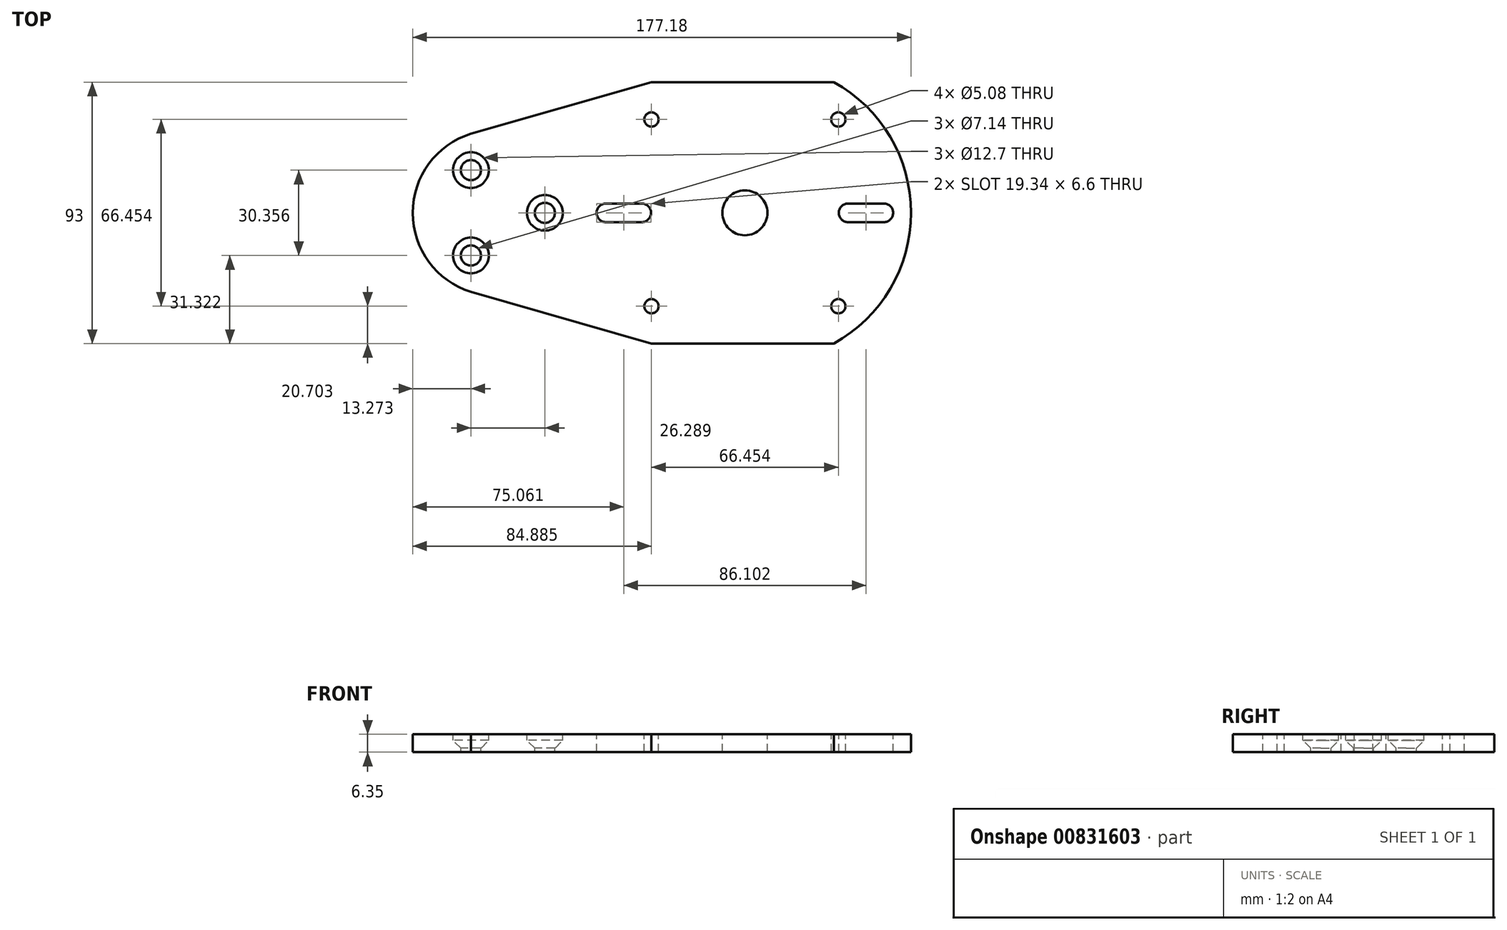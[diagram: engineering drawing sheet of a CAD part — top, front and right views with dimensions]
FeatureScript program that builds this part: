
annotation { "Feature Type Name" : "Feature", "Feature Type Description" : "" }
export const myFeature = defineFeature(function(context is Context, id is Id, definition is map)
    precondition{}
    {
        {
            var Q0;
            Q0=qCreatedBy(makeId("Top.planeOp"),FACE);
            var sketch = newSketch(context, id + "F0", { "sketchPlane" : qUnion([Q0])});
            skLineSegment(sketch, "E0", {"start": v(0, 0) * mm, "end": v(-58.93, 0) * mm, "construction": true});
            skPoint(sketch, "E1", {"position": v(-29.46, 0) * mm});
            skCircle(sketch, "E2", {"center": v(-29.46, 0) * mm, "radius": 29.46 * mm, "construction": true});
            skCircle(sketch, "E3", {"center": v(-29.46, 0) * mm, "radius": 17.53 * mm, "construction": true});
            skPoint(sketch, "E4", {"position": v(59.18, 0) * mm});
            skPoint(sketch, "E5", {"position": v(-11.94, 0) * mm});
            skCircle(sketch, "E6", {"center": v(59.18, 0) * mm, "radius": 19.05 * mm, "construction": true});
            skCircle(sketch, "E7", {"center": v(59.18, 0) * mm, "radius": 31.75 * mm, "construction": true});
            skCircle(sketch, "E8", {"center": v(-11.94, 0) * mm, "radius": 3.57 * mm});
            skCircle(sketch, "E9", {"center": v(-29.46, 0) * mm, "radius": 10.16 * mm, "construction": true});
            skArc(sketch, "E10", {"start": v(92.4, -46.5) * mm, "mid": v(116.33, 0) * mm, "end": v(92.4, 46.5) * mm, "construction": true});
            skPoint(sketch, "E11", {"position": v(59.18, 57.15) * mm});
            skPoint(sketch, "E12", {"position": v(59.18, -57.15) * mm});
            skLineSegment(sketch, "E13", {"start": v(90.93, 0) * mm, "end": v(118.25, 0) * mm, "construction": true});
            skCircle(sketch, "E14", {"center": v(59.18, 0) * mm, "radius": 47 * mm, "construction": true});
            skLineSegment(sketch, "E15", {"start": v(59.18, 0) * mm, "end": v(90.93, 0) * mm, "construction": true});
            skLineSegment(sketch, "E16", {"start": v(59.18, 0) * mm, "end": v(99.6, 40.41) * mm, "construction": true});
            skCircle(sketch, "E17", {"center": v(92.4, 33.23) * mm, "radius": 2.54 * mm});
            skCircle(sketch, "E18.2.0", {"center": v(25.96, 33.23) * mm, "radius": 2.54 * mm});
            skCircle(sketch, "E19", {"center": v(59.18, 0) * mm, "radius": 8 * mm});
            skCircle(sketch, "E20.1.4.0", {"center": v(25.96, -33.23) * mm, "radius": 2.54 * mm});
            skCircle(sketch, "E20.1.6.0", {"center": v(92.4, -33.23) * mm, "radius": 2.54 * mm});
            skPoint(sketch, "E21", {"position": v(25.96, 46.5) * mm});
            skPoint(sketch, "E22", {"position": v(25.96, -46.5) * mm});
            skLineSegment(sketch, "E23", {"start": v(25.96, 46.5) * mm, "end": v(90.78, 46.5) * mm});
            skLineSegment(sketch, "E24", {"start": v(25.96, -46.5) * mm, "end": v(90.78, -46.5) * mm});
            skArc(sketch, "E25.converted", {"start": v(92.4, 46.5) * mm, "mid": v(2.03, 0) * mm, "end": v(92.4, -46.5) * mm, "construction": true});
            skLineSegment(sketch, "E26", {"start": v(59.18, 0) * mm, "end": v(99.6, -40.41) * mm, "construction": true});
            skArc(sketch, "E27", {"start": v(90.78, -46.5) * mm, "mid": v(118.25, 0) * mm, "end": v(90.78, 46.5) * mm});
            skCircle(sketch, "E28", {"center": v(59.18, 0) * mm, "radius": 36.83 * mm, "construction": true});
            skCircle(sketch, "E29", {"center": v(59.18, 0) * mm, "radius": 49.53 * mm, "construction": true});
            skLineSegment(sketch, "E30", {"start": v(95.86, 3.3) * mm, "end": v(108.6, 3.3) * mm});
            skLineSegment(sketch, "E31", {"start": v(95.86, -3.3) * mm, "end": v(108.6, -3.3) * mm});
            skArc(sketch, "E32", {"start": v(108.6, 3.3) * mm, "mid": v(111.9, 0) * mm, "end": v(108.6, -3.3) * mm});
            skArc(sketch, "E33", {"start": v(95.86, 3.3) * mm, "mid": v(92.56, 0) * mm, "end": v(95.86, -3.3) * mm});
            skLineSegment(sketch, "E34.1.0", {"start": v(22.5, -3.3) * mm, "end": v(9.76, -3.3) * mm});
            skArc(sketch, "E34.1.1", {"start": v(22.5, -3.3) * mm, "mid": v(25.8, 0) * mm, "end": v(22.5, 3.3) * mm});
            skLineSegment(sketch, "E34.1.2", {"start": v(22.5, 3.3) * mm, "end": v(9.76, 3.3) * mm});
            skArc(sketch, "E34.1.3", {"start": v(9.76, -3.3) * mm, "mid": v(6.46, 0) * mm, "end": v(9.76, 3.3) * mm});
            skPoint(sketch, "E35", {"position": v(-38.23, 28.13) * mm});
            skLineSegment(sketch, "E36", {"start": v(25.96, 46.5) * mm, "end": v(-38.23, 28.13) * mm});
            skPoint(sketch, "E37", {"position": v(-38.23, -28.13) * mm});
            skLineSegment(sketch, "E38", {"start": v(25.96, -46.5) * mm, "end": v(-38.23, -28.13) * mm});
            skArc(sketch, "E39", {"start": v(-38.23, 28.13) * mm, "mid": v(-58.93, 0) * mm, "end": v(-38.23, -28.13) * mm});
            skCircle(sketch, "E40.1.0", {"center": v(-38.23, 15.18) * mm, "radius": 3.57 * mm});
            skCircle(sketch, "E40.2.0", {"center": v(-38.23, -15.18) * mm, "radius": 3.57 * mm});
            skSolve(sketch);
        }
        {
            var Q0;
            Q0=makeQuery(id+"F0.imprint","IMPRINT",FACE,{"disambiguationData":[TD([[makeQuery(id+"F0.imprint","IMPRINT",EDGE,{"derivedFrom":sQuery(id+"F0.wireOp",EDGE,"E8")}),-1.0]])]});
            extrude(context, id + "F1", {"entities" : qUnion([Q0]), "oppositeDirection" : true, "depth" : 6.35 * mm, "offsetDistance" : 25.4 * mm});
        }
        {
            var Q0;
            Q0=makeQuery(id+"F1.opExtrude","CAP_FACE",FACE,{"disambiguationData":[OSD([sQuery(id+"F0.wireOp",EDGE,"E8"),sQuery(id+"F0.wireOp",EDGE,"E17"),sQuery(id+"F0.wireOp",EDGE,"E18.2.0"),sQuery(id+"F0.wireOp",EDGE,"E19"),sQuery(id+"F0.wireOp",EDGE,"E20.1.4.0"),sQuery(id+"F0.wireOp",EDGE,"E20.1.6.0"),sQuery(id+"F0.wireOp",EDGE,"E23"),sQuery(id+"F0.wireOp",EDGE,"E24"),sQuery(id+"F0.wireOp",EDGE,"E27"),sQuery(id+"F0.wireOp",EDGE,"E30"),sQuery(id+"F0.wireOp",EDGE,"E31"),sQuery(id+"F0.wireOp",EDGE,"E32"),sQuery(id+"F0.wireOp",EDGE,"E33"),sQuery(id+"F0.wireOp",EDGE,"E34.1.0"),sQuery(id+"F0.wireOp",EDGE,"E34.1.1"),sQuery(id+"F0.wireOp",EDGE,"E34.1.2"),sQuery(id+"F0.wireOp",EDGE,"E34.1.3"),sQuery(id+"F0.wireOp",EDGE,"E36"),sQuery(id+"F0.wireOp",EDGE,"E38"),sQuery(id+"F0.wireOp",EDGE,"E39"),sQuery(id+"F0.wireOp",EDGE,"E40.1.0"),sQuery(id+"F0.wireOp",EDGE,"E40.2.0")])],"isStart":false});
            cPlane(context, id + "F2", {"entities" : qUnion([Q0]), "cplaneType" : CPlaneType.OFFSET, "offset" : 1.4 * mm, "oppositeDirection" : true, "width" : 152.4 * mm, "height" : 152.4 * mm});
        }
        {
            var Q0;
            Q0=qCreatedBy(id+"F2.planeOp",FACE);
            var sketch = newSketch(context, id + "F3", { "sketchPlane" : qUnion([Q0])});
            skCircle(sketch, "E41", {"center": v(-29.46, 0) * mm, "radius": 17.53 * mm, "construction": true});
            skCircle(sketch, "E42", {"center": v(-11.94, 0) * mm, "radius": 3.57 * mm});
            skCircle(sketch, "E43.1.0", {"center": v(-38.23, 15.18) * mm, "radius": 3.57 * mm});
            skCircle(sketch, "E43.2.0", {"center": v(-38.23, -15.18) * mm, "radius": 3.57 * mm});
            skSolve(sketch);
        }
        {
            var Q0;
            Q0=makeQuery(id+"F3.imprint","IMPRINT",FACE,{"disambiguationData":[TD([[makeQuery(id+"F3.imprint","IMPRINT",EDGE,{"derivedFrom":sQuery(id+"F3.wireOp",EDGE,"E43.1.0")}),1.0]])]});
            var Q1;
            Q1=makeQuery(id+"F3.imprint","IMPRINT",FACE,{"disambiguationData":[TD([[makeQuery(id+"F3.imprint","IMPRINT",EDGE,{"derivedFrom":sQuery(id+"F3.wireOp",EDGE,"E43.2.0")}),1.0]])]});
            var Q2;
            Q2=makeQuery(id+"F3.imprint","IMPRINT",FACE,{"disambiguationData":[TD([[makeQuery(id+"F3.imprint","IMPRINT",EDGE,{"derivedFrom":sQuery(id+"F3.wireOp",EDGE,"E42")}),1.0]])]});
            var Q3;
            Q3=makeQuery(id+"F1.opExtrude","CAP_FACE",FACE,{"disambiguationData":[OSD([sQuery(id+"F0.wireOp",EDGE,"E8"),sQuery(id+"F0.wireOp",EDGE,"E17"),sQuery(id+"F0.wireOp",EDGE,"E18.2.0"),sQuery(id+"F0.wireOp",EDGE,"E19"),sQuery(id+"F0.wireOp",EDGE,"E20.1.4.0"),sQuery(id+"F0.wireOp",EDGE,"E20.1.6.0"),sQuery(id+"F0.wireOp",EDGE,"E23"),sQuery(id+"F0.wireOp",EDGE,"E24"),sQuery(id+"F0.wireOp",EDGE,"E27"),sQuery(id+"F0.wireOp",EDGE,"E30"),sQuery(id+"F0.wireOp",EDGE,"E31"),sQuery(id+"F0.wireOp",EDGE,"E32"),sQuery(id+"F0.wireOp",EDGE,"E33"),sQuery(id+"F0.wireOp",EDGE,"E34.1.0"),sQuery(id+"F0.wireOp",EDGE,"E34.1.1"),sQuery(id+"F0.wireOp",EDGE,"E34.1.2"),sQuery(id+"F0.wireOp",EDGE,"E34.1.3"),sQuery(id+"F0.wireOp",EDGE,"E36"),sQuery(id+"F0.wireOp",EDGE,"E38"),sQuery(id+"F0.wireOp",EDGE,"E39"),sQuery(id+"F0.wireOp",EDGE,"E40.1.0"),sQuery(id+"F0.wireOp",EDGE,"E40.2.0")])],"isStart":true});
            extrude(context, id + "F4", {"entities" : qUnion([Q0, Q1, Q2]), "operationType" : NewBodyOperationType.REMOVE, "endBound" : BoundingType.UP_TO_SURFACE, "oppositeDirection" : true, "depth" : 2.03 * mm, "endBoundEntityFace" : qUnion([Q3]), "offsetDistance" : 25.4 * mm, "hasDraft" : true, "draftAngle" : 45 * degree});
        }
        {
            var Q0;
            Q0=makeQuery(id+"F1.opExtrude","CAP_FACE",FACE,{"disambiguationData":[OSD([sQuery(id+"F0.wireOp",EDGE,"E8"),sQuery(id+"F0.wireOp",EDGE,"E17"),sQuery(id+"F0.wireOp",EDGE,"E18.2.0"),sQuery(id+"F0.wireOp",EDGE,"E19"),sQuery(id+"F0.wireOp",EDGE,"E20.1.4.0"),sQuery(id+"F0.wireOp",EDGE,"E20.1.6.0"),sQuery(id+"F0.wireOp",EDGE,"E23"),sQuery(id+"F0.wireOp",EDGE,"E24"),sQuery(id+"F0.wireOp",EDGE,"E27"),sQuery(id+"F0.wireOp",EDGE,"E30"),sQuery(id+"F0.wireOp",EDGE,"E31"),sQuery(id+"F0.wireOp",EDGE,"E32"),sQuery(id+"F0.wireOp",EDGE,"E33"),sQuery(id+"F0.wireOp",EDGE,"E34.1.0"),sQuery(id+"F0.wireOp",EDGE,"E34.1.1"),sQuery(id+"F0.wireOp",EDGE,"E34.1.2"),sQuery(id+"F0.wireOp",EDGE,"E34.1.3"),sQuery(id+"F0.wireOp",EDGE,"E36"),sQuery(id+"F0.wireOp",EDGE,"E38"),sQuery(id+"F0.wireOp",EDGE,"E39"),sQuery(id+"F0.wireOp",EDGE,"E40.1.0"),sQuery(id+"F0.wireOp",EDGE,"E40.2.0")])],"isStart":true});
            var sketch = newSketch(context, id + "F5", { "sketchPlane" : qUnion([Q0])});
            skCircle(sketch, "E44", {"center": v(-11.94, 0) * mm, "radius": 6.35 * mm});
            skPoint(sketch, "E45.center", {"position": v(-29.46, 0) * mm});
            skCircle(sketch, "E46.1.0", {"center": v(-38.23, 15.18) * mm, "radius": 6.35 * mm});
            skCircle(sketch, "E46.2.0", {"center": v(-38.23, -15.18) * mm, "radius": 6.35 * mm});
            skSolve(sketch);
        }
        {
            var Q0;
            Q0=makeQuery(id+"F5.imprint","IMPRINT",FACE,{"disambiguationData":[TD([[makeQuery(id+"F5.imprint","IMPRINT",EDGE,{"derivedFrom":sQuery(id+"F5.wireOp",EDGE,"E44")}),-1.0]])]});
            var Q1;
            Q1=makeQuery(id+"F5.imprint","IMPRINT",FACE,{"disambiguationData":[TD([[makeQuery(id+"F5.imprint","IMPRINT",EDGE,{"derivedFrom":sQuery(id+"F5.wireOp",EDGE,"E46.1.0")}),-1.0]])]});
            var Q2;
            Q2=makeQuery(id+"F5.imprint","IMPRINT",FACE,{"disambiguationData":[TD([[makeQuery(id+"F5.imprint","IMPRINT",EDGE,{"derivedFrom":sQuery(id+"F5.wireOp",EDGE,"E46.2.0")}),-1.0]])]});
            var Q3;
            Q3=qCreatedBy(id+"F2.planeOp",FACE);
            extrude(context, id + "F6", {"entities" : qUnion([Q0, Q1, Q2]), "operationType" : NewBodyOperationType.ADD, "endBound" : BoundingType.UP_TO_SURFACE, "oppositeDirection" : true, "depth" : 25.4 * mm, "endBoundEntityFace" : qUnion([Q3]), "offsetDistance" : 25.4 * mm});
        }
    });
